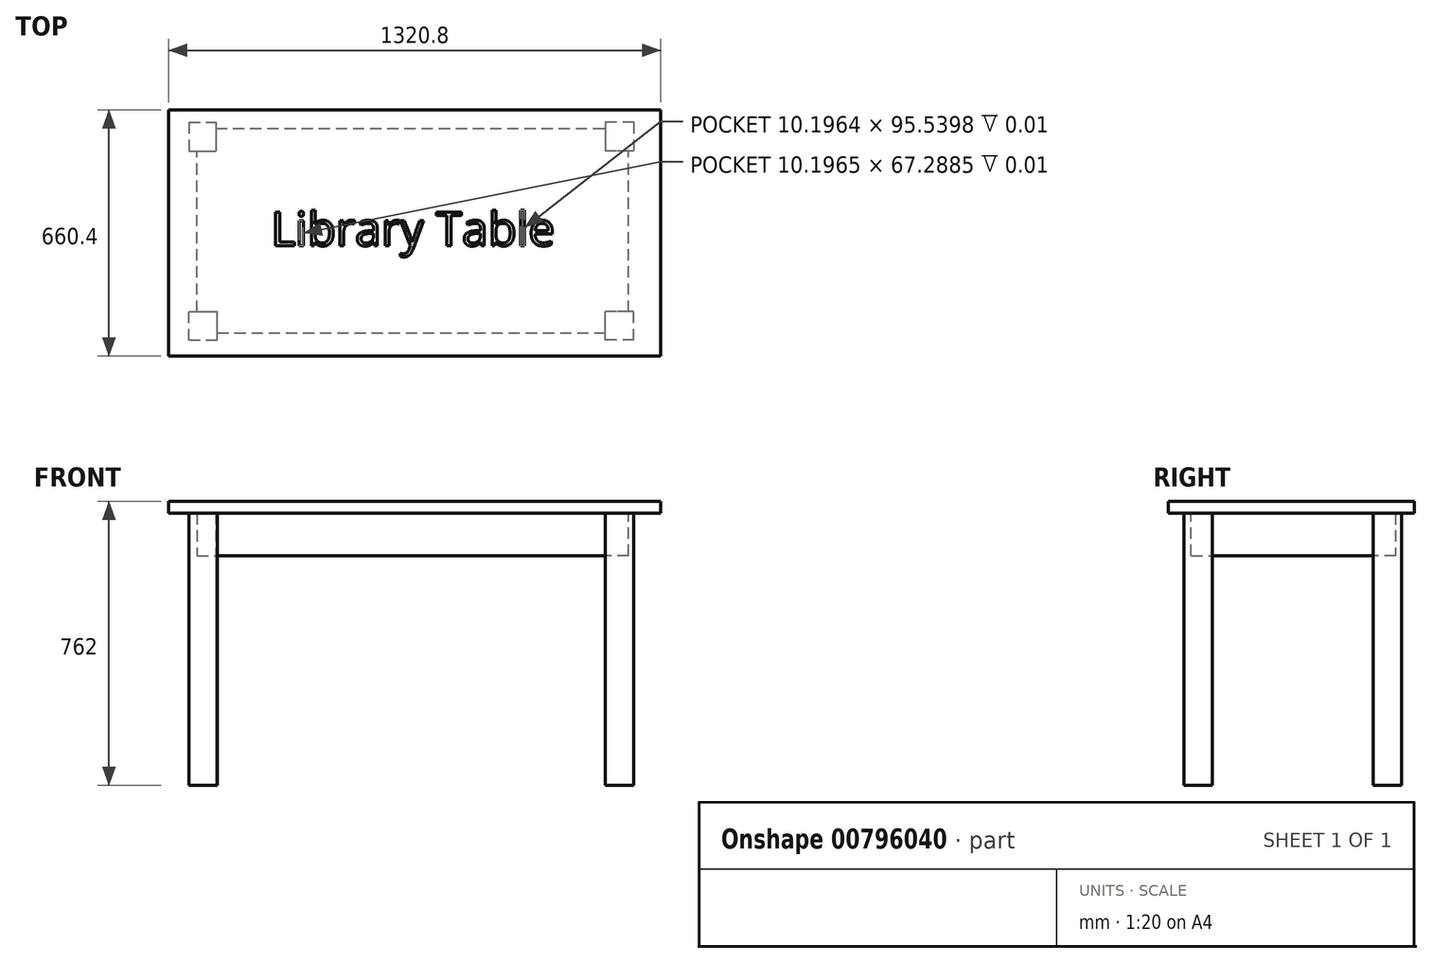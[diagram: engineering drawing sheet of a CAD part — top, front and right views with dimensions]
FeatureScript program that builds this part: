
annotation { "Feature Type Name" : "Feature", "Feature Type Description" : "" }
export const myFeature = defineFeature(function(context is Context, id is Id, definition is map)
    precondition{}
    {
        {
            var Q0;
            Q0=qCreatedBy(makeId("Top.planeOp"),FACE);
            var sketch = newSketch(context, id + "F0", { "sketchPlane" : qUnion([Q0])});
            skLineSegment(sketch, "E0.bottom", {"start": v(0, 0) * mm, "end": v(76.2, 0) * mm});
            skLineSegment(sketch, "E0.top", {"start": v(0, 76.2) * mm, "end": v(76.2, 76.2) * mm});
            skLineSegment(sketch, "E0.left", {"start": v(0, 0) * mm, "end": v(0, 76.2) * mm});
            skLineSegment(sketch, "E0.right", {"start": v(76.2, 0) * mm, "end": v(76.2, 76.2) * mm});
            skLineSegment(sketch, "E1.bottom", {"start": v(1193.8, 0) * mm, "end": v(1117.6, 0) * mm});
            skLineSegment(sketch, "E1.top", {"start": v(1193.8, 76.2) * mm, "end": v(1117.6, 76.2) * mm});
            skLineSegment(sketch, "E1.left", {"start": v(1193.8, 0) * mm, "end": v(1193.8, 76.2) * mm});
            skLineSegment(sketch, "E1.right", {"start": v(1117.6, 0) * mm, "end": v(1117.6, 76.2) * mm});
            skLineSegment(sketch, "E2.bottom", {"start": v(1193.8, 584.2) * mm, "end": v(1117.6, 584.2) * mm});
            skLineSegment(sketch, "E2.top", {"start": v(1193.8, 507.86) * mm, "end": v(1117.6, 507.86) * mm});
            skLineSegment(sketch, "E2.left", {"start": v(1193.8, 584.2) * mm, "end": v(1193.8, 507.86) * mm});
            skLineSegment(sketch, "E2.right", {"start": v(1117.6, 584.2) * mm, "end": v(1117.6, 507.86) * mm});
            skLineSegment(sketch, "E3.bottom", {"start": v(0, 584.2) * mm, "end": v(72.33, 584.2) * mm});
            skLineSegment(sketch, "E3.top", {"start": v(0, 507.86) * mm, "end": v(72.33, 507.86) * mm});
            skLineSegment(sketch, "E3.left", {"start": v(0, 584.2) * mm, "end": v(0, 507.86) * mm});
            skLineSegment(sketch, "E3.right", {"start": v(72.33, 584.2) * mm, "end": v(72.33, 507.86) * mm});
            skSolve(sketch);
        }
        {
            var Q0;
            Q0 = qSketchRegion(id + "F0", true);
            extrude(context, id + "F1", {"entities" : qUnion([Q0]), "depth" : 730.25 * mm, "offsetDistance" : 25.4 * mm});
        }
        {
            var Q0;
            Q0=makeQuery(id+"F1.opExtrude","CAP_FACE",FACE,{"disambiguationData":[OSD([sQuery(id+"F0.wireOp",EDGE,"E0.bottom"),sQuery(id+"F0.wireOp",EDGE,"E0.top"),sQuery(id+"F0.wireOp",EDGE,"E0.left"),sQuery(id+"F0.wireOp",EDGE,"E0.right")])],"isStart":false});
            var sketch = newSketch(context, id + "F2", { "sketchPlane" : qUnion([Q0])});
            skLineSegment(sketch, "E4.bottom", {"start": v(21.5, 19.3) * mm, "end": v(1180.26, 19.3) * mm});
            skLineSegment(sketch, "E4.top", {"start": v(21.5, 567.61) * mm, "end": v(1180.26, 567.61) * mm});
            skLineSegment(sketch, "E4.left", {"start": v(21.5, 19.3) * mm, "end": v(21.5, 567.61) * mm});
            skLineSegment(sketch, "E4.right", {"start": v(1180.26, 19.3) * mm, "end": v(1180.26, 567.61) * mm});
            skSolve(sketch);
        }
        {
            var Q0;
            Q0 = qSketchRegion(id + "F2", true);
            extrude(context, id + "F3", {"entities" : qUnion([Q0]), "oppositeDirection" : true, "depth" : 114.3 * mm, "offsetDistance" : 25.4 * mm});
        }
        {
            var Q0;
            Q0=makeQuery(id+"F1.opExtrude","CAP_FACE",FACE,{"disambiguationData":[OSD([sQuery(id+"F0.wireOp",EDGE,"E0.bottom"),sQuery(id+"F0.wireOp",EDGE,"E0.top"),sQuery(id+"F0.wireOp",EDGE,"E0.left"),sQuery(id+"F0.wireOp",EDGE,"E0.right")])],"isStart":false});
            var sketch = newSketch(context, id + "F4", { "sketchPlane" : qUnion([Q0])});
            skLineSegment(sketch, "E5.bottom", {"start": v(-54.92, -42.66) * mm, "end": v(1265.88, -42.66) * mm});
            skLineSegment(sketch, "E5.top", {"start": v(-54.92, 617.74) * mm, "end": v(1265.88, 617.74) * mm});
            skLineSegment(sketch, "E5.left", {"start": v(-54.92, -42.66) * mm, "end": v(-54.92, 617.74) * mm});
            skLineSegment(sketch, "E5.right", {"start": v(1265.88, -42.66) * mm, "end": v(1265.88, 617.74) * mm});
            skSolve(sketch);
        }
        {
            var Q0;
            Q0 = qSketchRegion(id + "F4", true);
            extrude(context, id + "F5", {"entities" : qUnion([Q0]), "operationType" : NewBodyOperationType.ADD, "depth" : 31.75 * mm, "offsetDistance" : 25.4 * mm});
        }
        {
            var Q0;
            Q0=makeQuery(id+"F5.opExtrude","CAP_FACE",FACE,{"disambiguationData":[OSD([sQuery(id+"F4.wireOp",EDGE,"E5.bottom"),sQuery(id+"F4.wireOp",EDGE,"E5.top"),sQuery(id+"F4.wireOp",EDGE,"E5.left"),sQuery(id+"F4.wireOp",EDGE,"E5.right")])],"isStart":false});
            var sketch = newSketch(context, id + "F6", { "sketchPlane" : qUnion([Q0])});
            skText(sketch, "E6", { "text": "Library Table", "fontName": "OpenSans-Regular.ttf"});
            const initialGuessF6  = {"E6": [0.2203, 0.25345, 1, 0, 0.09053]};
            skSetInitialGuess(sketch, initialGuessF6);
            skSolve(sketch);
        }
        {
            var Q0;
            Q0 = qSketchRegion(id + "F6", true);
            extrude(context, id + "F7", {"entities" : qUnion([Q0]), "operationType" : NewBodyOperationType.REMOVE, "oppositeDirection" : true, "depth" : 1 / 101.6 * mm, "offsetDistance" : 25.4 * mm});
        }
    });
